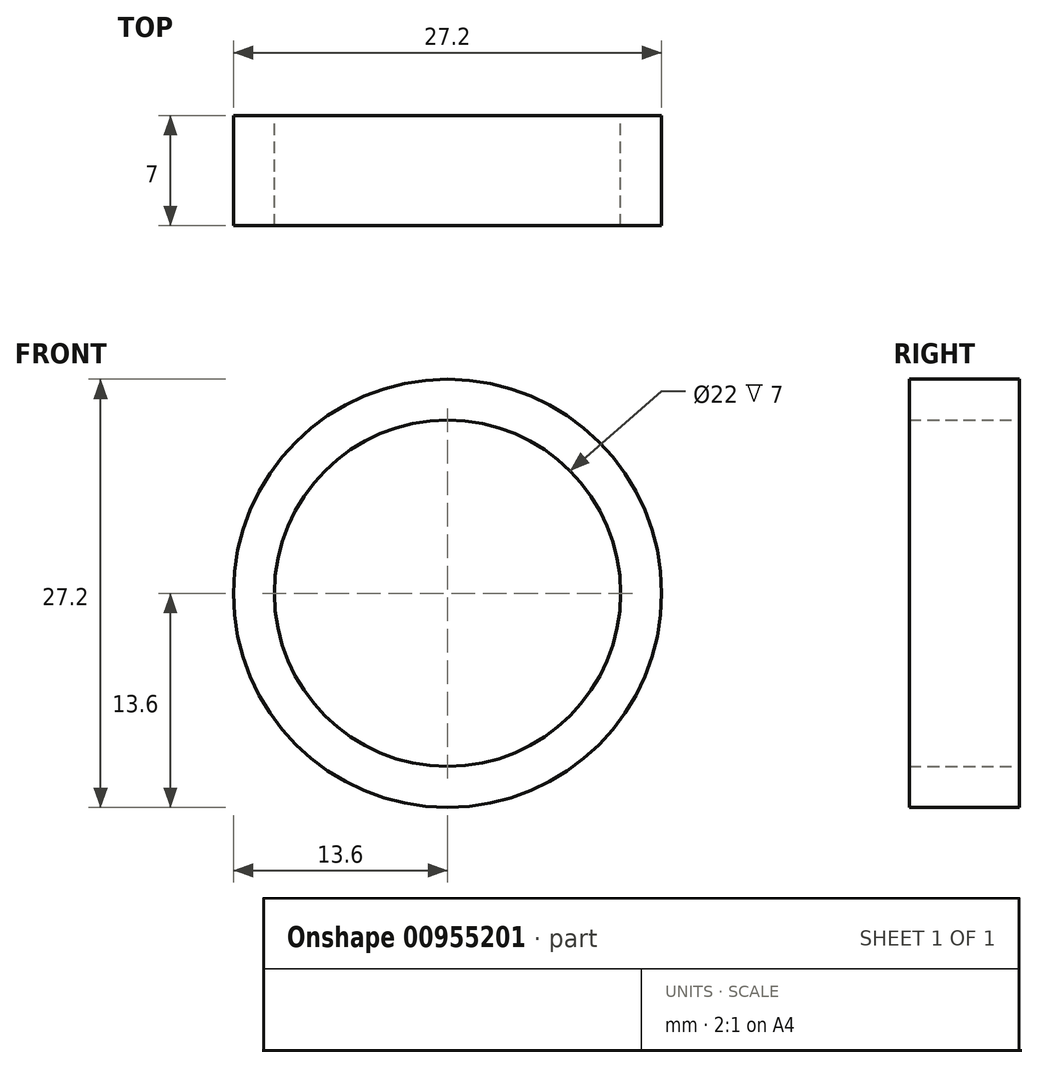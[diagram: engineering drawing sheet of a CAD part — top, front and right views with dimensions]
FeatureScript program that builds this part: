
annotation { "Feature Type Name" : "Feature", "Feature Type Description" : "" }
export const myFeature = defineFeature(function(context is Context, id is Id, definition is map)
    precondition{}
    {
        {
            var Q0;
            Q0=qCreatedBy(makeId("Front.planeOp"),FACE);
            var sketch = newSketch(context, id + "F0", { "sketchPlane" : qUnion([Q0])});
            skCircle(sketch, "E0", {"center": v(0, 0) * mm, "radius": 11 * mm});
            skCircle(sketch, "E1", {"center": v(0, 0) * mm, "radius": 13.6 * mm});
            skSolve(sketch);
        }
        {
            var Q0;
            Q0=makeQuery(id+"F0.imprint","IMPRINT",FACE,{"disambiguationData":[TD([[makeQuery(id+"F0.imprint","IMPRINT",EDGE,{"derivedFrom":sQuery(id+"F0.wireOp",EDGE,"E0")}),-1.0]])]});
            extrude(context, id + "F1", {"entities" : qUnion([Q0]), "depth" : 7 * mm, "offsetDistance" : 25 * mm});
        }
    });
